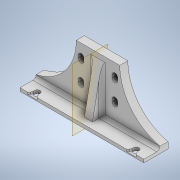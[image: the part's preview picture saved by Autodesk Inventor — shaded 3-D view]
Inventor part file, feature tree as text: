
AUTODESK INVENTOR PART (.ipt)
format: ipt  version: 2022.6 (Build 266554000, 554)  size: 241,152 bytes
history: native  units: mm
features: sketch x6, projected_geometry x5, extrude x4, hole x1, plane x1, rib x1, fillet x1, chamfer x1
ambient origin geometry x8: Origin, YZ Plane, XZ Plane, XY Plane, X Axis, Y Axis, Z Axis, Center Point
bodies: Solid1 (feature_tree)
feature tree (20):
  extrude  "Extrusion1"  Depth=2.0mm
  hole  "Hole1"  [1 undecoded]
  plane  "Work Plane1"
  rib  "Rib1"
  extrude  "Extrusion2"  Depth=77.0mm
  extrude  "Extrusion3"  [1 undecoded]
  fillet  "Fillet1"  Radius=6.0mm
  extrude  "Extrusion4"  Depth=2.0mm
  chamfer  "Chamfer1"  Distance=31.0mm
  sketch  "Sketch1"  dims[d0=35.0mm d1=2.0mm]
  sketch  "Sketch2"  dims[d2=15.0mm d3=5.0mm]
  projected_geometry  "Projected Loop1"
  sketch  "Sketch3"  dims[d4=77.0mm d5=0.0mm d6=3.0mm]
  projected_geometry  "Projected Loop2"
  sketch  "Sketch4"  dims[d7=61.5mm]
  projected_geometry  "Projected Loop3"
  sketch  "Sketch5"  dims[d8=3.4mm d9=6.0mm d10=15.9mm d11=1.2mm d12=90.0deg d13=8.0mm d14=20.594885mm d15=-38.5mm d16=6.0mm]
  projected_geometry  "Projected Loop4"
  sketch  "Sketch6"  dims[d17=30.0mm d18=1.0mm d19=5.0mm d20=0.0mm d21=0.0mm d22=1.0mm d23=1.0mm d24=25.0mm d25=31.0mm d26=0.0mm d27=0.0mm d28=21.0mm d29=13.0mm d30=13.0mm d31=1.8mm d32=3.4mm d33=20.0mm d35=21.0mm d36=20.0mm d38=13.0mm d41=0.0mm d42=0.0mm d43=2.0mm d47=1.0mm d48=1.3mm d49=0.0mm d50=4.0mm d51=1.0mm d52=2.0mm d53=45.0deg]
  projected_geometry  "Projected Loop5"
note: 2 required parameter values undecoded (feature->parameter linkage not recoverable at this tier; creation-order binding heuristic only, values carry confidence <= 0.55)
